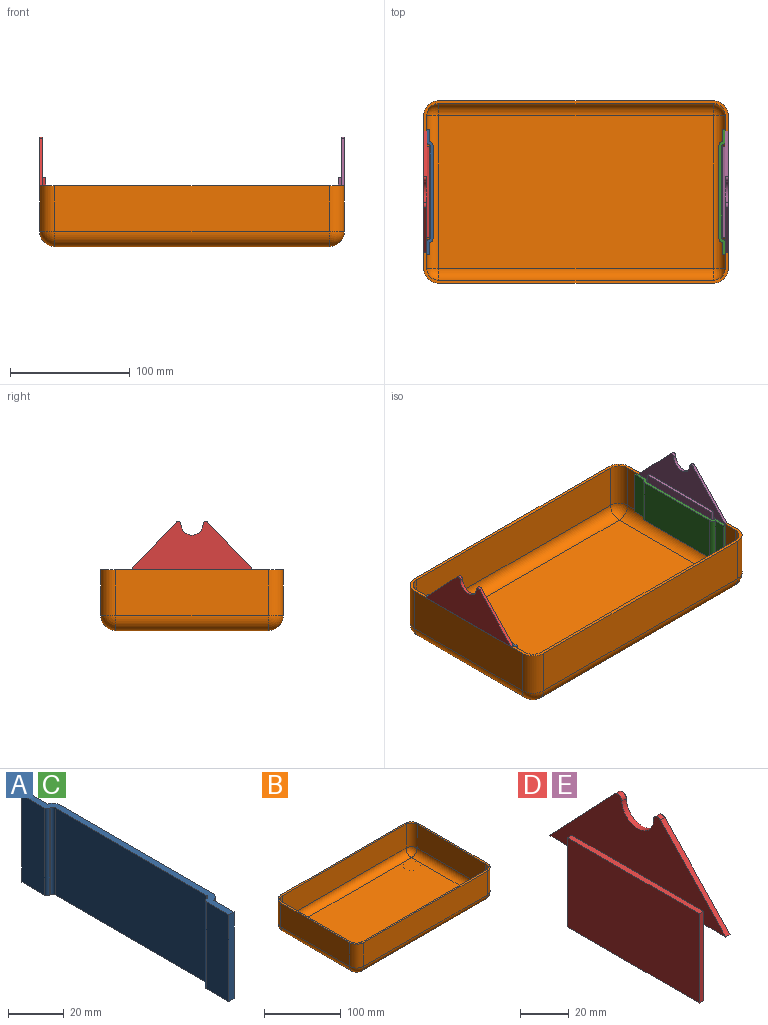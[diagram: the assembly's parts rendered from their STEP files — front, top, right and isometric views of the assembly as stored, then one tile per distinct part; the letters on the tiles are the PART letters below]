
ASSEMBLY  parts=5 mates=6
PART A: 18 faces, bbox 5.3x104.8x38.1 mm
  f0: plane 38.1x11.43mm, normal (-1,0,0), area 435.5mm2, adj f1,f15,f16,f17
  f1: cylinder r=1.27mm len=38.1mm, axis (0,0,-1), area 76mm2, adj f0,f2,f16,f17
  f2: plane 38.1x0.25mm, normal (0,-1,0), area 9.7mm2, adj f1,f3,f16,f17
  f3: cylinder r=1.27mm len=38.1mm, axis (0,0,-1), area 76mm2, adj f2,f4,f16,f17
  f4: plane 76.84x38.1mm, normal (-1,0,0), area 2927.4mm2, adj f3,f5,f16,f17
  f5: cylinder r=1.27mm len=38.1mm, axis (0,0,-1), area 76mm2, adj f4,f6,f16,f17
  f6: plane 38.1x0.25mm, normal (0,1,0), area 9.7mm2, adj f5,f7,f16,f17
  f7: cylinder r=1.27mm len=38.1mm, axis (0,0,-1), area 76mm2, adj f6,f8,f16,f17
  f8: plane 38.1x11.43mm, normal (-1,0,0), area 435.5mm2, adj f7,f9,f16,f17
  f9: plane 38.1x2.54mm, normal (0,-1,0), area 96.8mm2, adj f8,f10,f16,f17
  f10: plane 38.1x10.3mm, normal (1,0,0), area 392.4mm2, adj f9,f11,f16,f17
  f11: cylinder r=3.81mm len=38.1mm, axis (0,0,-1), area 188.8mm2, adj f10,f12,f16,f17
  f12: plane 76.84x38.1mm, normal (1,0,0), area 2927.4mm2, adj f11,f13,f16,f17
  f13: cylinder r=3.81mm len=38.1mm, axis (0,0,-1), area 188.8mm2, adj f12,f14,f16,f17
  f14: plane 38.1x10.3mm, normal (1,0,0), area 392.4mm2, adj f13,f15,f16,f17
  f15: plane 38.1x2.54mm, normal (0,1,0), area 96.8mm2, adj f0,f14,f16,f17
  f16: plane 104.78x5.33mm, normal (0,0,1), area 274.2mm2, adj f0,f1,f2,f3,f4,f5,f6,f7
  f17: plane 104.78x5.33mm, normal (0,0,-1), area 274.2mm2, adj f0,f1,f2,f3,f4,f5,f6,f7
PART B: 47 faces, bbox 254x152.4x50.8 mm
  f0: plane 12.7x12.7mm, normal (0,0,-1), area 34.6mm2, adj f8,f19,f26
  f1: plane 228.6x127mm, normal (0,0,-1), area 26866.9mm2, adj f6,f8,f14,f19,f26,f27,f28,f29
  f2: plane 12.7x12.7mm, normal (0,0,-1), area 34.6mm2, adj f8,f14,f28
  f3: plane 12.7x12.7mm, normal (0,0,-1), area 34.6mm2, adj f6,f14,f29
  f4: plane 254x152.4mm, normal (0,0,1), area 1988.9mm2, adj f5,f9,f10,f11,f12,f16,f17,f21
  f5: plane 228.6x38.1mm, normal (0,-1,0), area 8709.7mm2, adj f4,f6,f12,f21
  f6: cylinder r=12.7mm len=228.6mm, axis (-1,0,0), area 4560.4mm2, adj f1,f3,f5,f7,f13,f20
  f7: plane 12.7x12.7mm, normal (0,0,-1), area 34.6mm2, adj f6,f19,f27
  f8: cylinder r=12.7mm len=228.6mm, axis (-1,0,0), area 4560.4mm2, adj f0,f1,f2,f9,f15,f18
  f9: plane 228.6x38.1mm, normal (0,1,0), area 8709.7mm2, adj f4,f8,f16,f17
  f10: plane 127x38.1mm, normal (1,0,0), area 4838.7mm2, adj f4,f17,f19,f21
  f11: plane 127x38.1mm, normal (-1,0,0), area 4838.7mm2, adj f4,f12,f14,f16
  f12: cylinder r=12.7mm len=38.1mm, axis (0,0,-1), area 760.1mm2, adj f4,f5,f11,f13
  f13: sphere r=12.7mm, area 253.4mm2, adj f6,f12,f14
  f14: cylinder r=12.7mm len=127mm, axis (0,1,0), area 2533.5mm2, adj f1,f2,f3,f11,f13,f15
  f15: sphere r=12.7mm, area 253.4mm2, adj f8,f14,f16
  f16: cylinder r=12.7mm len=38.1mm, axis (0,0,1), area 760.1mm2, adj f4,f9,f11,f15
  f17: cylinder r=12.7mm len=38.1mm, axis (0,0,-1), area 760.1mm2, adj f4,f9,f10,f18
  f18: sphere r=12.7mm, area 253.4mm2, adj f8,f17,f19
  f19: cylinder r=12.7mm len=127mm, axis (0,-1,0), area 2533.5mm2, adj f0,f1,f7,f10,f18,f20
  f20: sphere r=12.7mm, area 253.4mm2, adj f6,f19,f21
  f21: cylinder r=12.7mm len=38.1mm, axis (0,0,1), area 760.1mm2, adj f4,f5,f10,f20
  f22: plane 22.23x22.23mm, normal (0,0,-1), area 387.9mm2, adj f29
  f23: plane 22.23x22.23mm, normal (0,0,-1), area 387.9mm2, adj f26
  f24: plane 22.23x22.23mm, normal (0,0,-1), area 387.9mm2, adj f27
  f25: plane 22.23x22.23mm, normal (0,0,-1), area 387.9mm2, adj f28
  f26: torus R=12.7mm, axis (0,0,1), area 183.1mm2, adj f0,f1,f23
  f27: torus R=12.7mm, axis (0,0,1), area 183.1mm2, adj f1,f7,f24
  f28: torus R=12.7mm, axis (0,0,1), area 183.1mm2, adj f1,f2,f25
  f29: torus R=12.7mm, axis (0,0,1), area 183.1mm2, adj f1,f3,f22
  f30: plane 228.6x38.1mm, normal (0,1,0), area 8709.7mm2, adj f4,f31,f37,f46
  f31: cylinder r=10.16mm len=228.6mm, axis (-1,0,0), area 3648.3mm2, adj f30,f32,f38,f45
  f32: plane 228.6x127mm, normal (0,0,1), area 29032.2mm2, adj f31,f33,f39,f44
  f33: cylinder r=10.16mm len=228.6mm, axis (-1,0,0), area 3648.3mm2, adj f32,f34,f40,f43
  f34: plane 228.6x38.1mm, normal (0,-1,0), area 8709.7mm2, adj f4,f33,f41,f42
  f35: plane 127x38.1mm, normal (-1,0,0), area 4838.7mm2, adj f4,f42,f44,f46
  f36: plane 127x38.1mm, normal (1,0,0), area 4838.7mm2, adj f4,f37,f39,f41
  f37: cylinder r=10.16mm len=38.1mm, axis (0,0,-1), area 608mm2, adj f4,f30,f36,f38
  f38: sphere r=10.16mm, area 162.1mm2, adj f31,f37,f39
  f39: cylinder r=10.16mm len=127mm, axis (0,1,0), area 2026.8mm2, adj f32,f36,f38,f40
  f40: sphere r=10.16mm, area 162.1mm2, adj f33,f39,f41
  f41: cylinder r=10.16mm len=38.1mm, axis (0,0,1), area 608mm2, adj f4,f34,f36,f40
  f42: cylinder r=10.16mm len=38.1mm, axis (0,0,-1), area 608mm2, adj f4,f34,f35,f43
  f43: sphere r=10.16mm, area 162.1mm2, adj f33,f42,f44
  f44: cylinder r=10.16mm len=127mm, axis (0,-1,0), area 2026.8mm2, adj f32,f35,f43,f45
  f45: sphere r=10.16mm, area 162.1mm2, adj f31,f44,f46
  f46: cylinder r=10.16mm len=38.1mm, axis (0,0,1), area 608mm2, adj f4,f30,f35,f45
PART C: same geometry as A
PART D: 14 faces, bbox 5.1x101.6x78.5 mm
  f0: plane 101.6x40.4mm, normal (-1,0,0), area 1881.6mm2, adj f1,f2,f3,f4,f5,f6,f10,f11
  f1: cylinder r=9.21mm len=18.42mm, axis (-1,0,0), area 73.5mm2, adj f0,f2,f6,f7
  f2: cylinder r=2.3mm len=3.97mm, axis (-1,0,0), area 13.9mm2, adj f0,f1,f3,f7
  f3: plane 39.68x37.62mm, normal (0,-0.73,0.69), area 138.9mm2, adj f0,f2,f4,f7
  f4: plane 101.6x2.54mm, normal (0,0,-1), area 258.1mm2, adj f0,f3,f5,f7,f8
  f5: plane 39.68x37.62mm, normal (0,0.73,0.69), area 138.9mm2, adj f0,f4,f6,f7
  f6: cylinder r=2.3mm len=3.97mm, axis (-1,0,0), area 13.9mm2, adj f0,f1,f5,f7
  f7: plane 101.6x40.4mm, normal (1,0,0), area 2379.3mm2, adj f1,f2,f3,f4,f5,f6
  f8: plane 76.2x38.1mm, normal (1,0,0), area 2903.2mm2, adj f4,f9,f10,f12
  f9: plane 76.2x2.54mm, normal (0,0,-1), area 193.5mm2, adj f8,f10,f12,f13
  f10: plane 44.63x2.54mm, normal (0,1,0), area 113.4mm2, adj f0,f8,f9,f11,f13
  f11: plane 76.2x2.54mm, normal (0,0,1), area 193.5mm2, adj f0,f10,f12,f13
  f12: plane 44.63x2.54mm, normal (0,-1,0), area 113.4mm2, adj f0,f8,f9,f11,f13
  f13: plane 76.2x44.63mm, normal (-1,0,0), area 3400.9mm2, adj f9,f10,f11,f12
PART E: same geometry as D
PLACE A t=(-107.73,105.65,41.36)mm fixed
PLACE B t=(16.73,29.54,28.66)mm fixed
PLACE C rot(axis=(0,1,0),180deg) t=(141.19,105.74,79.46)mm fixed
PLACE D rot(axis=(0,0,1),180deg) t=(-107.73,105.74,79.46)mm
PLACE E t=(141.19,105.74,79.46)mm
MATE planar C.f17 <-> B.f4  axis (0,0,1) through (137.8,105.74,79.46)mm
MATE planar A.f0 <-> B.f36  axis (-1,0,0) through (-107.73,152.32,60.41)mm
MATE planar B.f4 <-> A.f16  axis (0,0,1) through (16.73,105.74,79.46)mm
MATE planar B.f35 <-> C.f0  axis (-1,0,0) through (141.19,169.24,60.41)mm
MATE fastened B.f4 <-> E.f4  axis (0,0,1) through (141.19,105.74,79.46)mm
MATE fastened D.f4 <-> B.f4  axis (0,0,-1) through (-107.73,105.74,79.46)mm
